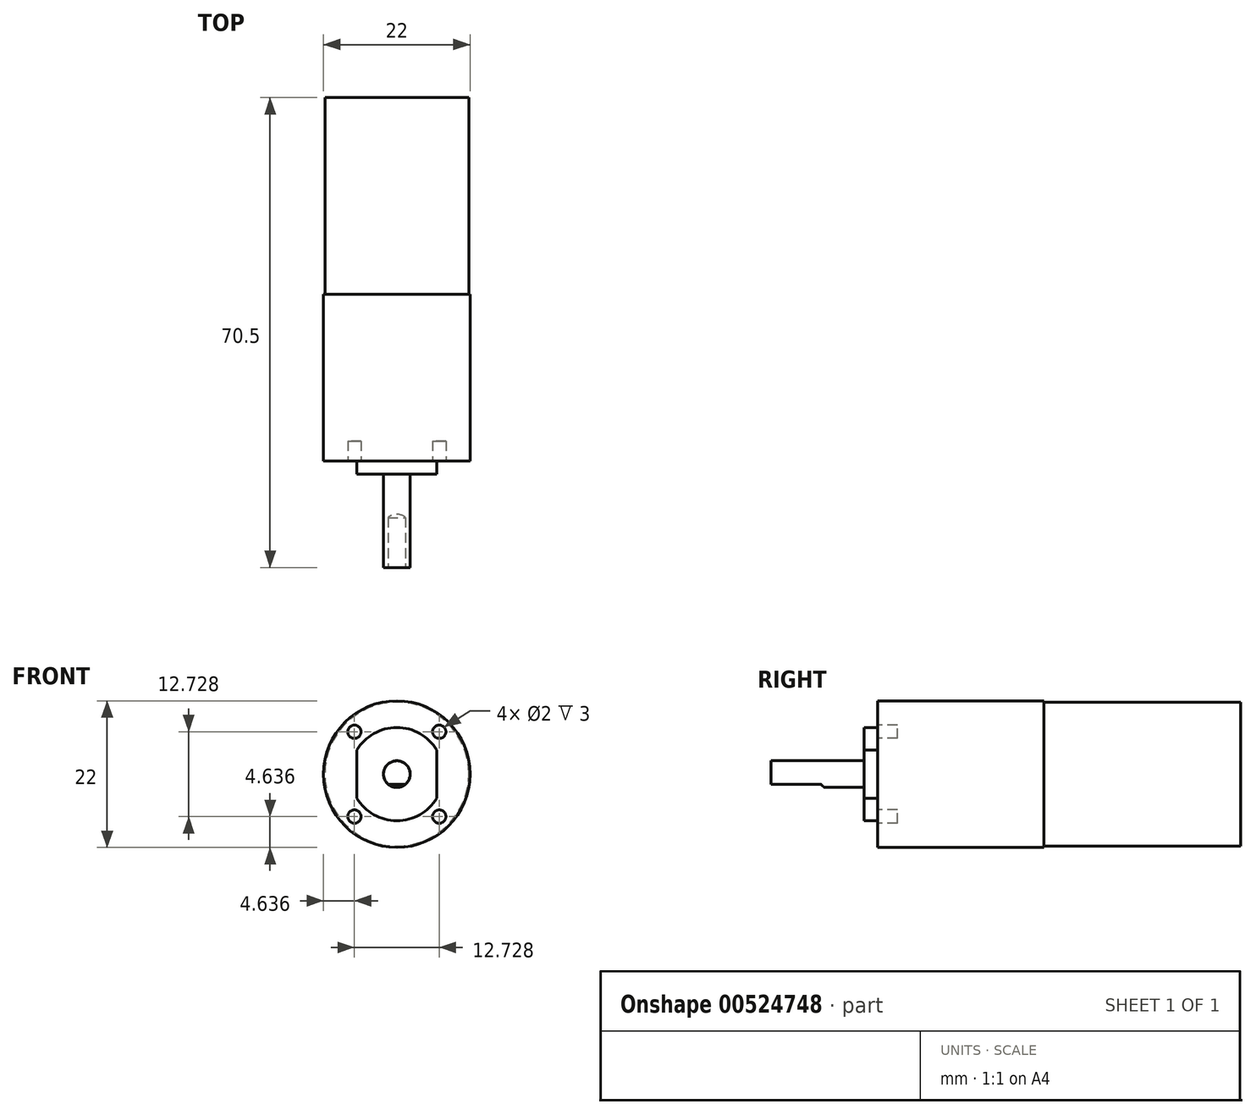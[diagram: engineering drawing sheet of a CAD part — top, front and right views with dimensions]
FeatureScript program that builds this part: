
annotation { "Feature Type Name" : "Feature", "Feature Type Description" : "" }
export const myFeature = defineFeature(function(context is Context, id is Id, definition is map)
    precondition{}
    {
        {
            var Q0;
            Q0=qCreatedBy(makeId("Front.planeOp"),FACE);
            var sketch = newSketch(context, id + "F0", { "sketchPlane" : qUnion([Q0])});
            skCircle(sketch, "E0", {"center": v(0, 0) * mm, "radius": 11 * mm});
            skSolve(sketch);
        }
        {
            var Q0;
            Q0 = qSketchRegion(id + "F0", true);
            extrude(context, id + "F1", {"entities" : qUnion([Q0]), "oppositeDirection" : true, "depth" : 25 * mm, "offsetDistance" : 25.4 * mm});
        }
        {
            var Q0;
            Q0=makeQuery(id+"F1.opExtrude","CAP_FACE",FACE,{"disambiguationData":[OSD([sQuery(id+"F0.wireOp",EDGE,"E0")])],"isStart":false});
            var sketch = newSketch(context, id + "F2", { "sketchPlane" : qUnion([Q0])});
            skCircle(sketch, "E1", {"center": v(0, 0) * mm, "radius": 10.8 * mm});
            skSolve(sketch);
        }
        {
            var Q0;
            Q0 = qSketchRegion(id + "F2", true);
            extrude(context, id + "F3", {"entities" : qUnion([Q0]), "operationType" : NewBodyOperationType.ADD, "depth" : 29.5 * mm, "offsetDistance" : 25.4 * mm});
        }
        {
            var Q0;
            Q0=makeQuery(id+"F1.opExtrude","CAP_FACE",FACE,{"disambiguationData":[OSD([sQuery(id+"F0.wireOp",EDGE,"E0")])],"isStart":true});
            var sketch = newSketch(context, id + "F4", { "sketchPlane" : qUnion([Q0])});
            skArc(sketch, "E2", {"start": v(6, 3.6) * mm, "mid": v(0, 7) * mm, "end": v(-6, 3.6) * mm});
            skLineSegment(sketch, "E3.bottom", {"start": v(6, -3.6) * mm, "end": v(-6, -3.6) * mm, "construction": true});
            skLineSegment(sketch, "E3.top", {"start": v(6, 3.6) * mm, "end": v(-6, 3.6) * mm, "construction": true});
            skLineSegment(sketch, "E3.left", {"start": v(6, -3.6) * mm, "end": v(6, 3.6) * mm});
            skLineSegment(sketch, "E3.right", {"start": v(-6, -3.6) * mm, "end": v(-6, 3.6) * mm});
            skArc(sketch, "E4.trimOffspring", {"start": v(-6, -3.6) * mm, "mid": v(0, -7) * mm, "end": v(6, -3.6) * mm});
            skSolve(sketch);
        }
        {
            var Q0;
            Q0 = qSketchRegion(id + "F4", true);
            extrude(context, id + "F5", {"entities" : qUnion([Q0]), "operationType" : NewBodyOperationType.ADD, "depth" : 2 * mm, "offsetDistance" : 25.4 * mm});
        }
        {
            var Q0;
            Q0=makeQuery(id+"F5.opExtrude","CAP_FACE",FACE,{"disambiguationData":[OSD([sQuery(id+"F4.wireOp",EDGE,"E2"),sQuery(id+"F4.wireOp",EDGE,"E3.left"),sQuery(id+"F4.wireOp",EDGE,"E3.right"),sQuery(id+"F4.wireOp",EDGE,"E4.trimOffspring")])],"isStart":false});
            var sketch = newSketch(context, id + "F6", { "sketchPlane" : qUnion([Q0])});
            skCircle(sketch, "E5", {"center": v(0, 0) * mm, "radius": 2 * mm});
            skSolve(sketch);
        }
        {
            var Q0;
            Q0 = qSketchRegion(id + "F6", true);
            extrude(context, id + "F7", {"entities" : qUnion([Q0]), "operationType" : NewBodyOperationType.ADD, "depth" : 14 * mm, "offsetDistance" : 25.4 * mm});
        }
        {
            var Q0;
            Q0=makeQuery(id+"F7.opExtrude","CAP_FACE",FACE,{"disambiguationData":[OSD([sQuery(id+"F6.wireOp",EDGE,"E5")])],"isStart":false});
            var sketch = newSketch(context, id + "F8", { "sketchPlane" : qUnion([Q0])});
            skLineSegment(sketch, "E6", {"start": v(1.32, -1.5) * mm, "end": v(-1.32, -1.5) * mm});
            skLineSegment(sketch, "E7", {"start": v(0, -1.5) * mm, "end": v(0, 2) * mm, "construction": true});
            skArc(sketch, "E8.0", {"start": v(-1.32, -1.5) * mm, "mid": v(0, -2) * mm, "end": v(1.32, -1.5) * mm});
            skSolve(sketch);
        }
        {
            var Q0;
            Q0 = qSketchRegion(id + "F8", true);
            extrude(context, id + "F9", {"entities" : qUnion([Q0]), "operationType" : NewBodyOperationType.REMOVE, "oppositeDirection" : true, "depth" : 8 * mm, "offsetDistance" : 25.4 * mm});
        }
        {
            var Q0;
            Q0=makeQuery(id+"F9.boolean.opBoolean","COPY",EDGE,{"derivedFrom":makeQuery(id+"F9.opExtrude","CAP_EDGE",EDGE,{"disambiguationData":[OSD([sQuery(id+"F8.wireOp",EDGE,"E6")])],"isStart":false})});
            chamfer(context, id + "F10", {"entities" : qUnion([Q0]), "width" : .5 * mm, "tangentPropagation" : true});
        }
        {
            var Q0;
            Q0=makeQuery(id+"F1.opExtrude","CAP_FACE",FACE,{"disambiguationData":[OSD([sQuery(id+"F0.wireOp",EDGE,"E0")])],"isStart":true});
            var sketch = newSketch(context, id + "F11", { "sketchPlane" : qUnion([Q0])});
            skCircle(sketch, "E9", {"center": v(0, 0) * mm, "radius": 9 * mm, "construction": true});
            skLineSegment(sketch, "E10.bottom", {"start": v(6.36, -6.36) * mm, "end": v(-6.36, -6.36) * mm, "construction": true});
            skLineSegment(sketch, "E10.top", {"start": v(6.36, 6.36) * mm, "end": v(-6.36, 6.36) * mm, "construction": true});
            skLineSegment(sketch, "E10.left", {"start": v(6.36, -6.36) * mm, "end": v(6.36, 6.36) * mm, "construction": true});
            skLineSegment(sketch, "E10.right", {"start": v(-6.36, -6.36) * mm, "end": v(-6.36, 6.36) * mm, "construction": true});
            skCircle(sketch, "E11", {"center": v(6.36, -6.36) * mm, "radius": 1 * mm});
            skCircle(sketch, "E12", {"center": v(-6.36, -6.36) * mm, "radius": 1 * mm});
            skCircle(sketch, "E13", {"center": v(-6.36, 6.36) * mm, "radius": 1 * mm});
            skCircle(sketch, "E14", {"center": v(6.36, 6.36) * mm, "radius": 1 * mm});
            skSolve(sketch);
        }
        {
            var Q0;
            Q0 = qSketchRegion(id + "F11", true);
            extrude(context, id + "F12", {"entities" : qUnion([Q0]), "operationType" : NewBodyOperationType.REMOVE, "oppositeDirection" : true, "depth" : 3 * mm, "offsetDistance" : 25.4 * mm});
        }
    });
